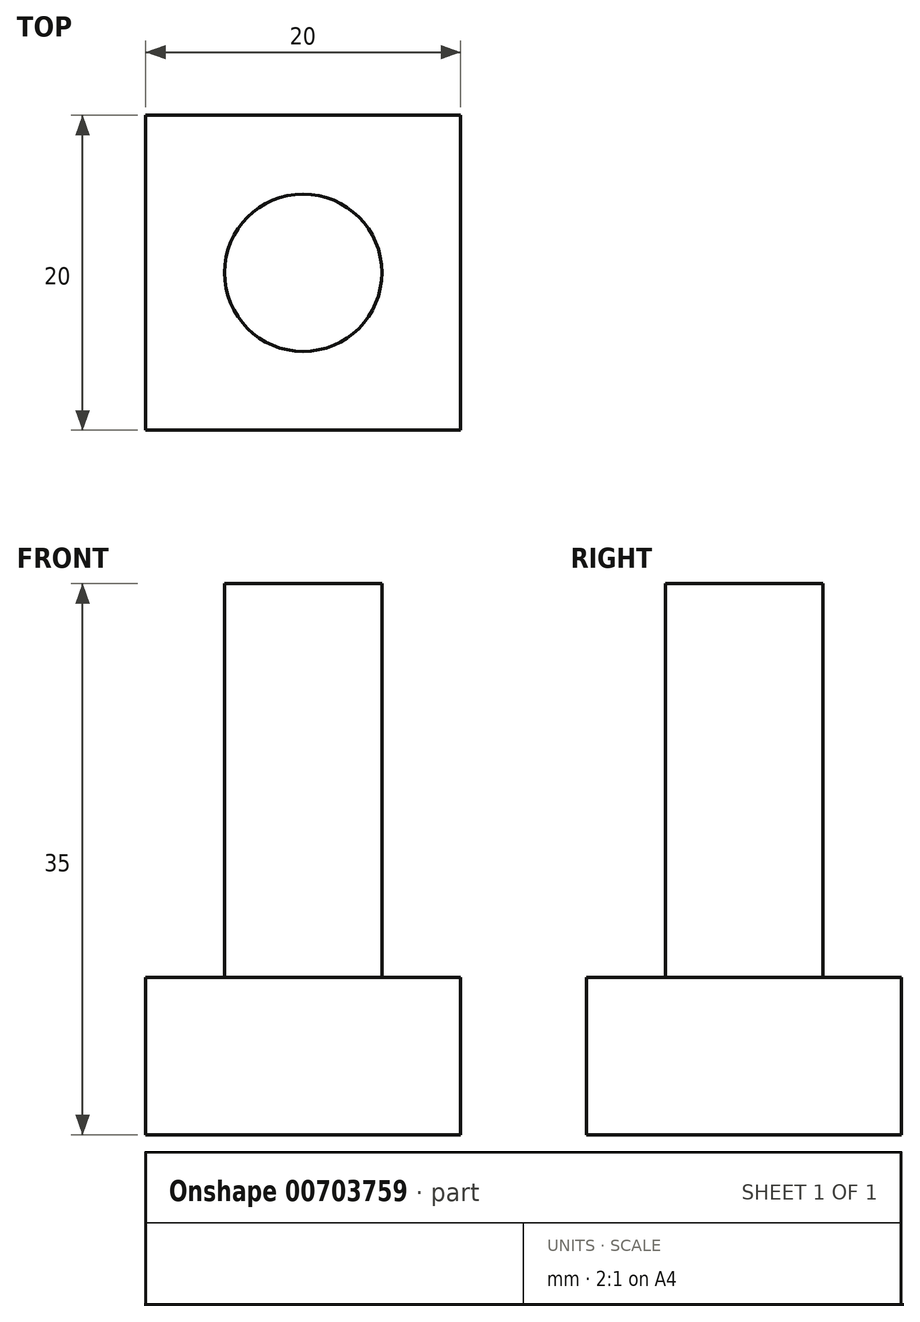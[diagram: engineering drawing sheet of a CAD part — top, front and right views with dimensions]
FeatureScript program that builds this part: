
annotation { "Feature Type Name" : "Feature", "Feature Type Description" : "" }
export const myFeature = defineFeature(function(context is Context, id is Id, definition is map)
    precondition{}
    {
        {
            var Q0;
            Q0=qCreatedBy(makeId("Top.planeOp"),FACE);
            var sketch = newSketch(context, id + "F0", { "sketchPlane" : qUnion([Q0])});
            skLineSegment(sketch, "E0.bottom", {"start": v(10, 10) * mm, "end": v(-10, 10) * mm});
            skLineSegment(sketch, "E0.top", {"start": v(10, -10) * mm, "end": v(-10, -10) * mm});
            skLineSegment(sketch, "E0.left", {"start": v(10, 10) * mm, "end": v(10, -10) * mm});
            skLineSegment(sketch, "E0.right", {"start": v(-10, 10) * mm, "end": v(-10, -10) * mm});
            skPoint(sketch, "E0.middle", {"position": v(0, 0) * mm});
            skSolve(sketch);
        }
        {
            var Q0;
            Q0=qSketchRegion(id+"F0",true);
            extrude(context, id + "F1", {"entities" : qUnion([Q0]), "depth" : 10 * mm, "offsetDistance" : 25 * mm});
        }
        {
            var Q0;
            Q0=makeQuery(id+"F1.opExtrude","CAP_FACE",FACE,{"disambiguationData":[OSD([sQuery(id+"F0.wireOp",EDGE,"E0.bottom"),sQuery(id+"F0.wireOp",EDGE,"E0.top"),sQuery(id+"F0.wireOp",EDGE,"E0.left"),sQuery(id+"F0.wireOp",EDGE,"E0.right")])],"isStart":false});
            var sketch = newSketch(context, id + "F2", { "sketchPlane" : qUnion([Q0])});
            skCircle(sketch, "E1", {"center": v(0, 0) * mm, "radius": 5 * mm});
            skSolve(sketch);
        }
        {
            var Q0;
            Q0=qSketchRegion(id+"F2",true);
            extrude(context, id + "F3", {"entities" : qUnion([Q0]), "operationType" : NewBodyOperationType.ADD, "depth" : 25 * mm, "offsetDistance" : 25 * mm});
        }
    });
